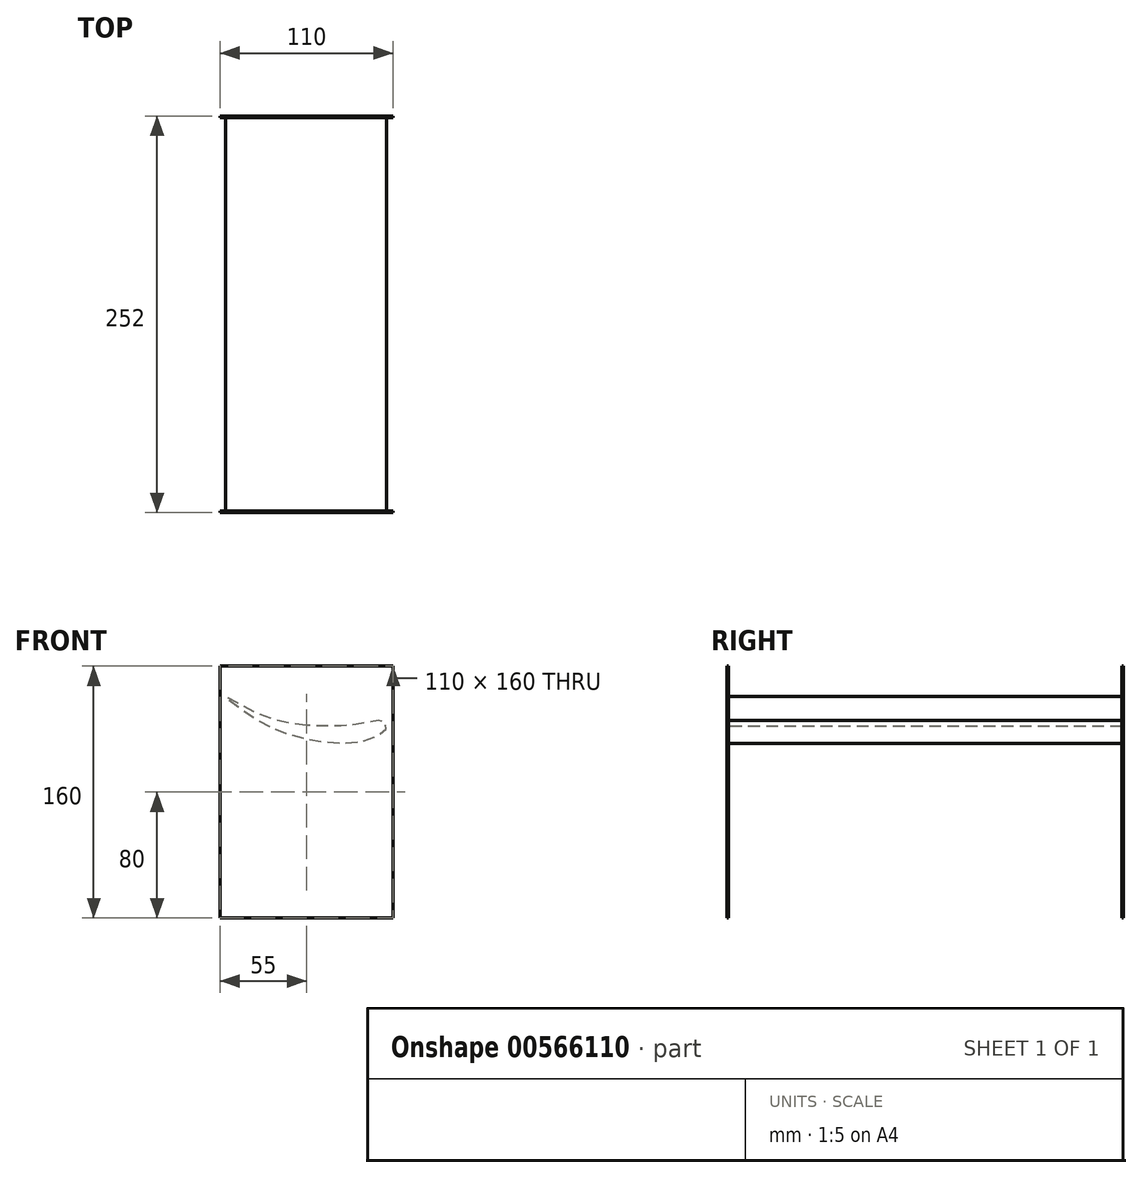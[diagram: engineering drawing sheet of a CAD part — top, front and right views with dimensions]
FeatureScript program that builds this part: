
annotation { "Feature Type Name" : "Feature", "Feature Type Description" : "" }
export const myFeature = defineFeature(function(context is Context, id is Id, definition is map)
    precondition{}
    {
        {
            var Q0;
            Q0=qCreatedBy(makeId("Front.planeOp"),FACE);
            var sketch = newSketch(context, id + "F0", { "sketchPlane" : qUnion([Q0])});
            skLineSegment(sketch, "E0.bottom", {"start": v(55, 37.5) * mm, "end": v(-55, 37.5) * mm});
            skLineSegment(sketch, "E0.top", {"start": v(55, -37.5) * mm, "end": v(-55, -37.5) * mm});
            skLineSegment(sketch, "E0.left", {"start": v(55, 37.5) * mm, "end": v(55, -37.5) * mm});
            skLineSegment(sketch, "E0.right", {"start": v(-55, 37.5) * mm, "end": v(-55, -37.5) * mm});
            skPoint(sketch, "E0.middle", {"position": v(0, 0) * mm});
            skLineSegment(sketch, "E1.bottom", {"start": v(-55, -37.5) * mm, "end": v(55, -37.5) * mm});
            skLineSegment(sketch, "E1.top", {"start": v(-55, -122.5) * mm, "end": v(55, -122.5) * mm});
            skLineSegment(sketch, "E1.left", {"start": v(-55, -37.5) * mm, "end": v(-55, -122.5) * mm});
            skLineSegment(sketch, "E1.right", {"start": v(55, -37.5) * mm, "end": v(55, -122.5) * mm});
            skSolve(sketch);
        }
        {
            var Q0;
            Q0=makeQuery(id+"F0.imprint","IMPRINT",FACE,{"disambiguationData":[TD([[makeQuery(id+"F0.imprint","IMPRINT",EDGE,{"derivedFrom":sQuery(id+"F0.wireOp",EDGE,"E0.bottom")}),1.0]])]});
            extrude(context, id + "F1", {"entities" : qUnion([Q0]), "depth" : 1 * mm, "offsetDistance" : 25 * mm});
        }
        {
            var Q0;
            Q0=makeQuery(id+"F1.opExtrude","CAP_FACE",FACE,{"disambiguationData":[OSD([sQuery(id+"F0.wireOp",EDGE,"E0.bottom"),sQuery(id+"F0.wireOp",EDGE,"E0.top"),sQuery(id+"F0.wireOp",EDGE,"E0.left"),sQuery(id+"F0.wireOp",EDGE,"E0.right")])],"isStart":true});
            var sketch = newSketch(context, id + "F2", { "sketchPlane" : qUnion([Q0])});
            skFitSpline(sketch, "E2", {"points": [v(0, 0) * mm, v(30.8, 7.23) * mm, v(51.57, 18.2) * mm, v(32.9, 4.43) * mm, v(9.33, -6.3) * mm, v(-28.93, -11.2) * mm, v(-50.17, -2.8) * mm, v(-49.93, 2.1) * mm, v(-44.1, 2.8) * mm, v(-28.93, 0) * mm, v(0, 0) * mm]});
            skSolve(sketch);
        }
        {
            var Q0;
            Q0=makeQuery(id+"F2.imprint","IMPRINT",FACE,{"disambiguationData":[TD([[makeQuery(id+"F2.imprint","IMPRINT",EDGE,{"derivedFrom":sQuery(id+"F2.wireOp",EDGE,"E2")}),-1.0]])]});
            extrude(context, id + "F3", {"entities" : qUnion([Q0]), "operationType" : NewBodyOperationType.ADD, "depth" : 250 * mm, "offsetDistance" : 25 * mm});
        }
        {
            var Q0;
            Q0 = qSketchRegion(id + "F0", true);
            extrude(context, id + "F4", {"entities" : qUnion([Q0]), "operationType" : NewBodyOperationType.ADD, "depth" : 1 * mm, "offsetDistance" : 25 * mm});
        }
        {
            var Q0;
            Q0=makeQuery(id+"F3.opExtrude","CAP_FACE",FACE,{"disambiguationData":[OSD([sQuery(id+"F2.wireOp",EDGE,"E2")])],"isStart":false});
            var sketch = newSketch(context, id + "F5", { "sketchPlane" : qUnion([Q0])});
            skLineSegment(sketch, "E3.bottom", {"start": v(55, -37.5) * mm, "end": v(-55, -37.5) * mm});
            skLineSegment(sketch, "E3.top", {"start": v(55, 37.5) * mm, "end": v(-55, 37.5) * mm});
            skLineSegment(sketch, "E3.left", {"start": v(55, -37.5) * mm, "end": v(55, 37.5) * mm});
            skLineSegment(sketch, "E3.right", {"start": v(-55, -37.5) * mm, "end": v(-55, 37.5) * mm});
            skPoint(sketch, "E3.middle", {"position": v(0, 0) * mm});
            skLineSegment(sketch, "E4.bottom", {"start": v(-55, -37.5) * mm, "end": v(55, -37.5) * mm});
            skLineSegment(sketch, "E4.top", {"start": v(-55, -122.5) * mm, "end": v(55, -122.5) * mm});
            skLineSegment(sketch, "E4.left", {"start": v(-55, -37.5) * mm, "end": v(-55, -122.5) * mm});
            skLineSegment(sketch, "E4.right", {"start": v(55, -37.5) * mm, "end": v(55, -122.5) * mm});
            skSolve(sketch);
        }
        {
            var Q0;
            Q0 = qSketchRegion(id + "F5", true);
            extrude(context, id + "F6", {"entities" : qUnion([Q0]), "operationType" : NewBodyOperationType.ADD, "depth" : 1 * mm, "offsetDistance" : 25 * mm});
        }
        {
            var Q0;
            Q0 = qSketchRegion(id + "F5", true);
            extrude(context, id + "F7", {"entities" : qUnion([Q0]), "operationType" : NewBodyOperationType.ADD, "depth" : 1 * mm, "offsetDistance" : 25 * mm});
        }
    });
